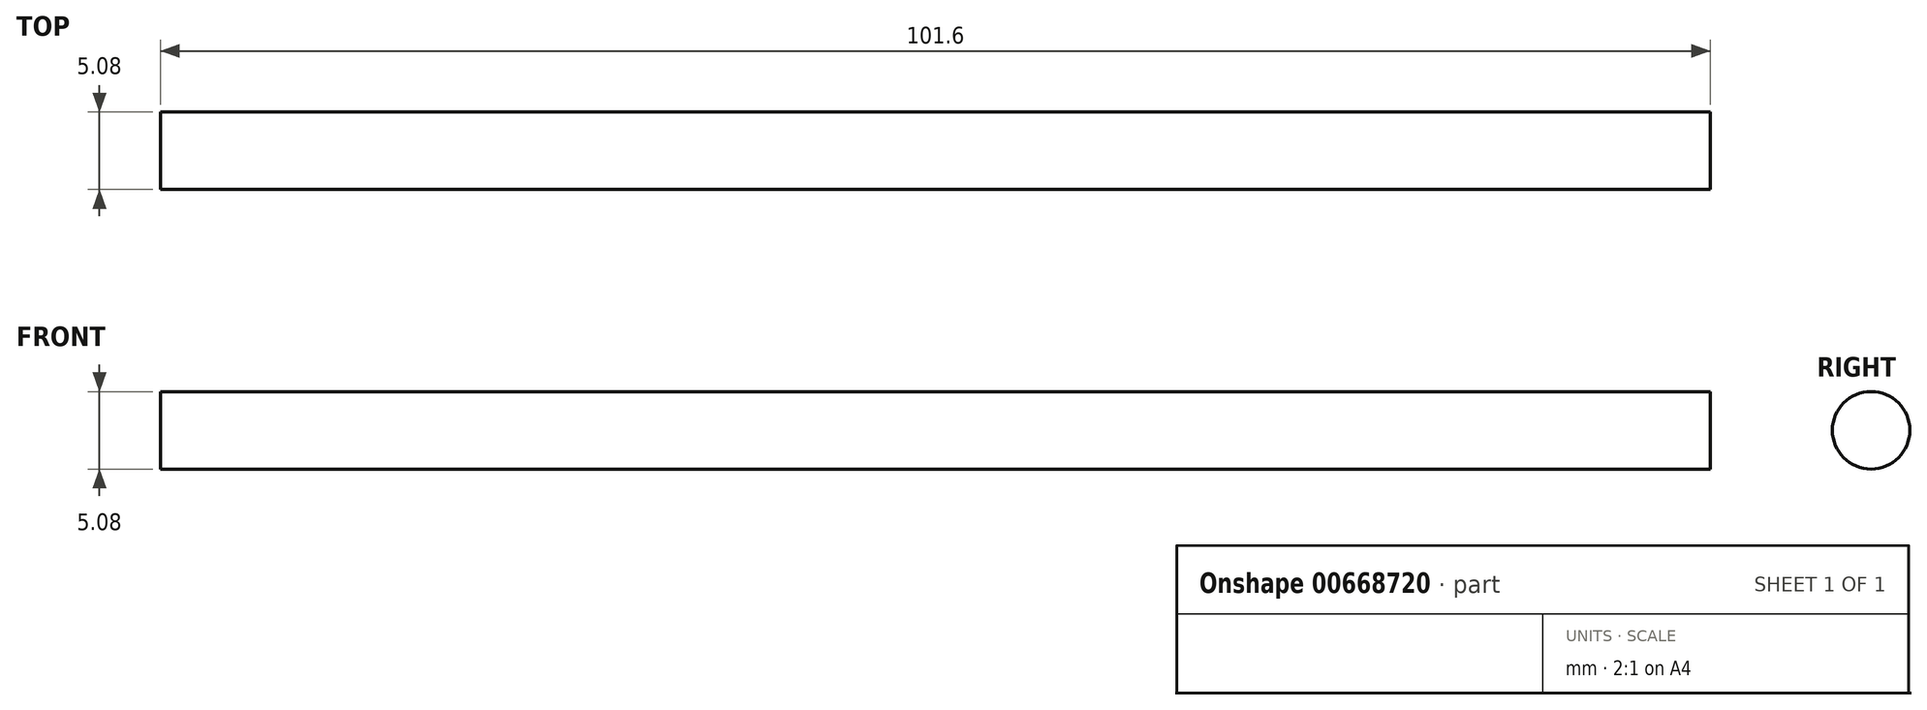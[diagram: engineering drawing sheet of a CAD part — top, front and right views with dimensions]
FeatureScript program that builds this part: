
annotation { "Feature Type Name" : "Feature", "Feature Type Description" : "" }
export const myFeature = defineFeature(function(context is Context, id is Id, definition is map)
    precondition{}
    {
        {
            var Q0;
            Q0=qCreatedBy(makeId("Right.planeOp"),FACE);
            var sketch = newSketch(context, id + "F0", { "sketchPlane" : qUnion([Q0])});
            skCircle(sketch, "E0", {"center": v(0, 0) * mm, "radius": 2.54 * mm});
            skSolve(sketch);
        }
        {
            var Q0;
            Q0 = qSketchRegion(id + "F0", true);
            extrude(context, id + "F1", {"entities" : qUnion([Q0]), "depth" : 101.6 * mm, "offsetDistance" : 25.4 * mm});
        }
    });
